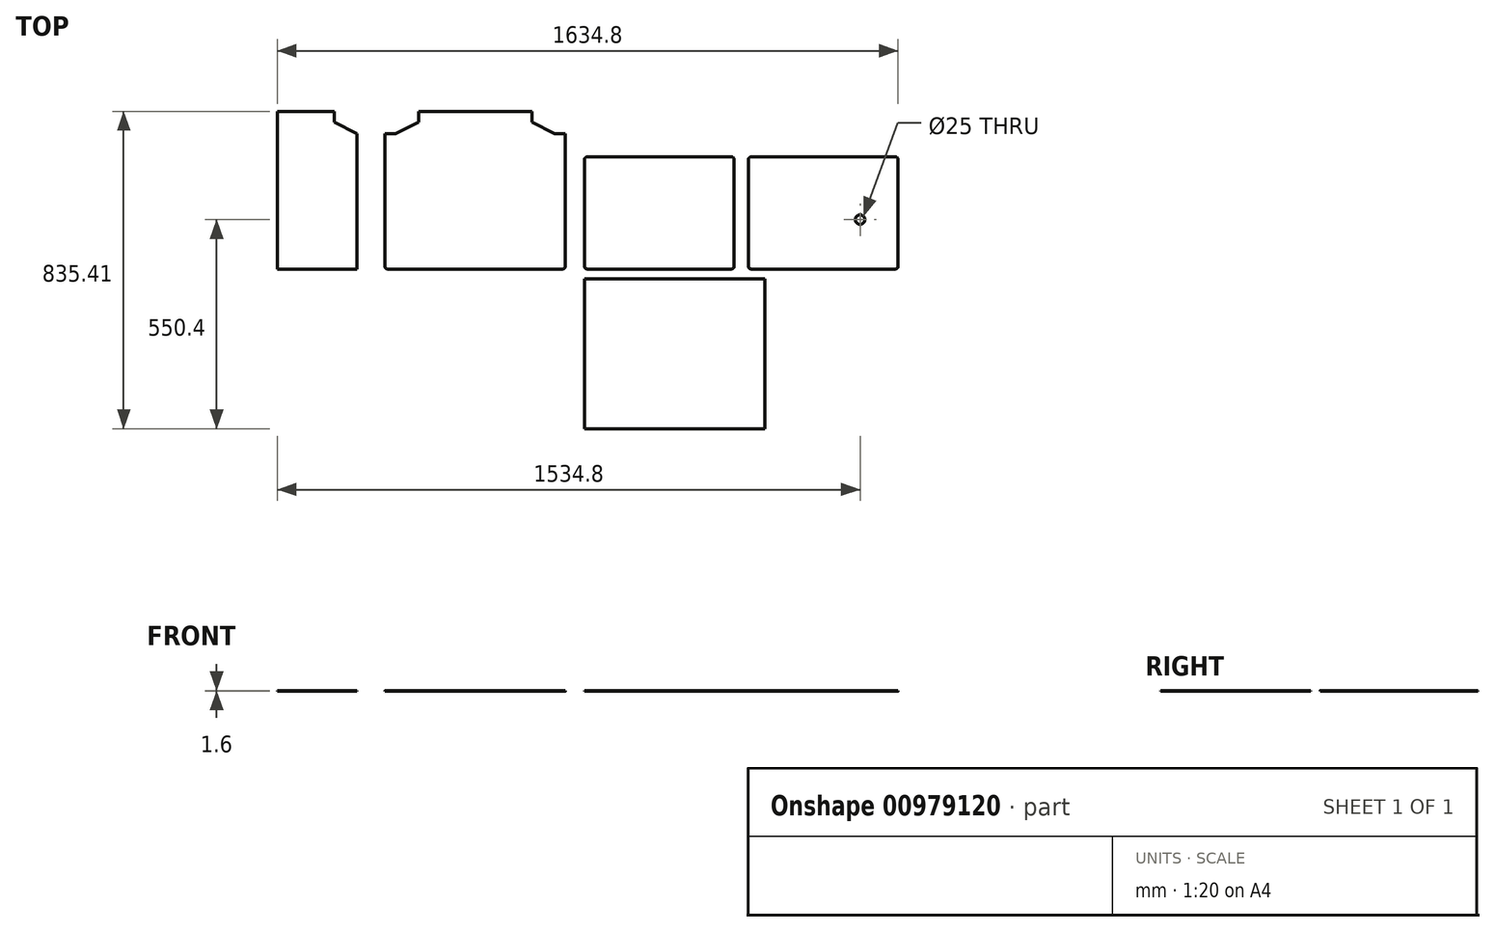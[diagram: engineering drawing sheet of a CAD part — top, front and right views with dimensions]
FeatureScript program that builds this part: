
annotation { "Feature Type Name" : "Feature", "Feature Type Description" : "" }
export const myFeature = defineFeature(function(context is Context, id is Id, definition is map)
    precondition{}
    {
        {
            var Q0;
            Q0=qCreatedBy(makeId("Top.planeOp"),FACE);
            var sketch = newSketch(context, id + "F0", { "sketchPlane" : qUnion([Q0])});
            skLineSegment(sketch, "E0.bottom", {"start": v(413.05, 295) * mm, "end": v(31.75, 295) * mm});
            skLineSegment(sketch, "E0.top", {"start": v(413.05, 0) * mm, "end": v(31.75, 0) * mm});
            skLineSegment(sketch, "E0.left", {"start": v(419.4, 288.65) * mm, "end": v(419.4, 6.35) * mm});
            skLineSegment(sketch, "E0.right", {"start": v(25.4, 288.65) * mm, "end": v(25.4, 6.35) * mm});
            skLineSegment(sketch, "E1.bottom", {"start": v(463.55, 0) * mm, "end": v(844.85, 0) * mm});
            skLineSegment(sketch, "E1.top", {"start": v(463.55, 295) * mm, "end": v(844.85, 295) * mm});
            skLineSegment(sketch, "E1.left", {"start": v(457.2, 6.35) * mm, "end": v(457.2, 288.65) * mm});
            skLineSegment(sketch, "E1.right", {"start": v(851.2, 6.35) * mm, "end": v(851.2, 288.65) * mm});
            skPoint(sketch, "E2.visualSharp", {"position": v(25.4, 295) * mm});
            skArc(sketch, "E2.filletArc", {"start": v(31.75, 295) * mm, "mid": v(27.26, 293.14) * mm, "end": v(25.4, 288.65) * mm});
            skPoint(sketch, "E3.visualSharp", {"position": v(419.4, 295) * mm});
            skArc(sketch, "E3.filletArc", {"start": v(419.4, 288.65) * mm, "mid": v(417.54, 293.14) * mm, "end": v(413.05, 295) * mm});
            skPoint(sketch, "E4.visualSharp", {"position": v(419.4, 0) * mm});
            skArc(sketch, "E4.filletArc", {"start": v(413.05, 0) * mm, "mid": v(417.54, 1.86) * mm, "end": v(419.4, 6.35) * mm});
            skPoint(sketch, "E5.visualSharp", {"position": v(25.4, 0) * mm});
            skArc(sketch, "E5.filletArc", {"start": v(25.4, 6.35) * mm, "mid": v(27.26, 1.86) * mm, "end": v(31.75, 0) * mm});
            skPoint(sketch, "E6.visualSharp", {"position": v(457.2, 0) * mm});
            skArc(sketch, "E6.filletArc", {"start": v(457.2, 6.35) * mm, "mid": v(459.06, 1.86) * mm, "end": v(463.55, 0) * mm});
            skPoint(sketch, "E7.visualSharp", {"position": v(457.2, 295) * mm});
            skArc(sketch, "E7.filletArc", {"start": v(463.55, 295) * mm, "mid": v(459.06, 293.14) * mm, "end": v(457.2, 288.65) * mm});
            skPoint(sketch, "E8.visualSharp", {"position": v(851.2, 295) * mm});
            skArc(sketch, "E8.filletArc", {"start": v(851.2, 288.65) * mm, "mid": v(849.34, 293.14) * mm, "end": v(844.85, 295) * mm});
            skPoint(sketch, "E9.visualSharp", {"position": v(851.2, 0) * mm});
            skArc(sketch, "E9.filletArc", {"start": v(844.85, 0) * mm, "mid": v(849.34, 1.86) * mm, "end": v(851.2, 6.35) * mm});
            skLineSegment(sketch, "E10", {"start": v(457.2, 0) * mm, "end": v(851.2, 0) * mm, "construction": true});
            skLineSegment(sketch, "E11", {"start": v(419.4, 0) * mm, "end": v(25.4, 0) * mm, "construction": true});
            skCircle(sketch, "E12", {"center": v(751.2, 130) * mm, "radius": 12.5 * mm});
            skLineSegment(sketch, "E13.bottom", {"start": v(-31.75, 0) * mm, "end": v(-494.05, 0) * mm});
            skLineSegment(sketch, "E13.top", {"start": v(-31.75, 415) * mm, "end": v(-494.05, 415) * mm});
            skLineSegment(sketch, "E13.left", {"start": v(-25.4, 6.35) * mm, "end": v(-25.4, 408.65) * mm});
            skLineSegment(sketch, "E13.right", {"start": v(-500.4, 6.35) * mm, "end": v(-500.4, 408.65) * mm});
            skPoint(sketch, "E14.visualSharp", {"position": v(-500.4, 415) * mm});
            skArc(sketch, "E14.filletArc", {"start": v(-494.05, 415) * mm, "mid": v(-498.54, 413.14) * mm, "end": v(-500.4, 408.65) * mm});
            skPoint(sketch, "E15.visualSharp", {"position": v(-25.4, 415) * mm});
            skArc(sketch, "E15.filletArc", {"start": v(-25.4, 408.65) * mm, "mid": v(-27.26, 413.14) * mm, "end": v(-31.75, 415) * mm});
            skPoint(sketch, "E16.visualSharp", {"position": v(-25.4, 0) * mm});
            skArc(sketch, "E16.filletArc", {"start": v(-31.75, 0) * mm, "mid": v(-27.26, 1.86) * mm, "end": v(-25.4, 6.35) * mm});
            skPoint(sketch, "E17.visualSharp", {"position": v(-500.4, 0) * mm});
            skArc(sketch, "E17.filletArc", {"start": v(-500.4, 6.35) * mm, "mid": v(-498.54, 1.86) * mm, "end": v(-494.05, 0) * mm});
            skLineSegment(sketch, "E18.bottom", {"start": v(-500.4, 415) * mm, "end": v(-412.12, 415) * mm});
            skLineSegment(sketch, "E18.top", {"start": v(-500.4, 387.06) * mm, "end": v(-412.12, 387.06) * mm});
            skLineSegment(sketch, "E18.left", {"start": v(-500.4, 415) * mm, "end": v(-500.4, 387.06) * mm});
            skLineSegment(sketch, "E18.right", {"start": v(-412.12, 415) * mm, "end": v(-412.12, 387.06) * mm});
            skLineSegment(sketch, "E19.bottom", {"start": v(-25.4, 415) * mm, "end": v(-113.67, 415) * mm});
            skLineSegment(sketch, "E19.top", {"start": v(-25.4, 387.06) * mm, "end": v(-113.67, 387.06) * mm});
            skLineSegment(sketch, "E19.left", {"start": v(-25.4, 415) * mm, "end": v(-25.4, 387.06) * mm});
            skLineSegment(sketch, "E19.right", {"start": v(-113.67, 415) * mm, "end": v(-113.67, 387.06) * mm});
            skLineSegment(sketch, "E20.bottom", {"start": v(-500.4, 387.06) * mm, "end": v(-472.46, 387.06) * mm});
            skLineSegment(sketch, "E20.top", {"start": v(-500.4, 356.58) * mm, "end": v(-472.46, 356.58) * mm});
            skLineSegment(sketch, "E20.left", {"start": v(-500.4, 387.06) * mm, "end": v(-500.4, 356.58) * mm});
            skLineSegment(sketch, "E20.right", {"start": v(-472.46, 387.06) * mm, "end": v(-472.46, 356.58) * mm});
            skLineSegment(sketch, "E21.bottom", {"start": v(-25.4, 387.06) * mm, "end": v(-53.34, 387.06) * mm});
            skLineSegment(sketch, "E21.top", {"start": v(-25.4, 356.58) * mm, "end": v(-53.34, 356.58) * mm});
            skLineSegment(sketch, "E21.left", {"start": v(-25.4, 387.06) * mm, "end": v(-25.4, 356.58) * mm});
            skLineSegment(sketch, "E21.right", {"start": v(-53.34, 387.06) * mm, "end": v(-53.34, 356.58) * mm});
            skLineSegment(sketch, "E22", {"start": v(-472.46, 356.58) * mm, "end": v(-412.12, 387.06) * mm});
            skLineSegment(sketch, "E23", {"start": v(-113.67, 387.06) * mm, "end": v(-53.34, 356.58) * mm});
            skLineSegment(sketch, "E24.bottom", {"start": v(-546.1, 0) * mm, "end": v(-1021.1, 0) * mm});
            skLineSegment(sketch, "E24.top", {"start": v(-546.1, 415.01) * mm, "end": v(-1021.1, 415.01) * mm});
            skLineSegment(sketch, "E24.left", {"start": v(-546.1, 0) * mm, "end": v(-546.1, 415.01) * mm});
            skLineSegment(sketch, "E24.right", {"start": v(-1021.1, 0) * mm, "end": v(-1021.1, 415.01) * mm});
            skLineSegment(sketch, "E25", {"start": v(-783.6, 415.01) * mm, "end": v(-783.6, 0) * mm});
            skLineSegment(sketch, "E26.bottom", {"start": v(-546.1, 415.01) * mm, "end": v(-634.38, 415.01) * mm});
            skLineSegment(sketch, "E26.top", {"start": v(-546.1, 387.07) * mm, "end": v(-634.38, 387.07) * mm});
            skLineSegment(sketch, "E26.left", {"start": v(-546.1, 415.01) * mm, "end": v(-546.1, 387.07) * mm});
            skLineSegment(sketch, "E26.right", {"start": v(-634.38, 415.01) * mm, "end": v(-634.38, 387.07) * mm});
            skLineSegment(sketch, "E27.bottom", {"start": v(-546.1, 387.07) * mm, "end": v(-574.04, 387.07) * mm});
            skLineSegment(sketch, "E27.top", {"start": v(-546.1, 356.6) * mm, "end": v(-574.04, 356.6) * mm});
            skLineSegment(sketch, "E27.left", {"start": v(-546.1, 387.07) * mm, "end": v(-546.1, 356.6) * mm});
            skLineSegment(sketch, "E27.right", {"start": v(-574.04, 387.07) * mm, "end": v(-574.04, 356.6) * mm});
            skLineSegment(sketch, "E28.bottom", {"start": v(-1021.1, 415.01) * mm, "end": v(-932.83, 415.01) * mm});
            skLineSegment(sketch, "E28.top", {"start": v(-1021.1, 387.07) * mm, "end": v(-932.83, 387.07) * mm});
            skLineSegment(sketch, "E28.left", {"start": v(-1021.1, 415.01) * mm, "end": v(-1021.1, 387.07) * mm});
            skLineSegment(sketch, "E28.right", {"start": v(-932.83, 415.01) * mm, "end": v(-932.83, 387.07) * mm});
            skLineSegment(sketch, "E29.bottom", {"start": v(-1021.1, 387.07) * mm, "end": v(-993.17, 387.07) * mm});
            skLineSegment(sketch, "E29.top", {"start": v(-1021.1, 356.6) * mm, "end": v(-993.17, 356.6) * mm});
            skLineSegment(sketch, "E29.left", {"start": v(-1021.1, 387.07) * mm, "end": v(-1021.1, 356.6) * mm});
            skLineSegment(sketch, "E29.right", {"start": v(-993.17, 387.07) * mm, "end": v(-993.17, 356.6) * mm});
            skLineSegment(sketch, "E30", {"start": v(-993.17, 356.6) * mm, "end": v(-932.83, 387.07) * mm});
            skLineSegment(sketch, "E31", {"start": v(-634.38, 387.07) * mm, "end": v(-574.04, 356.6) * mm});
            skLineSegment(sketch, "E32.bottom", {"start": v(-574.04, 356.6) * mm, "end": v(-546.1, 356.6) * mm});
            skLineSegment(sketch, "E32.top", {"start": v(-574.04, 0) * mm, "end": v(-546.1, 0) * mm});
            skLineSegment(sketch, "E32.left", {"start": v(-574.04, 356.6) * mm, "end": v(-574.04, 0) * mm});
            skLineSegment(sketch, "E32.right", {"start": v(-546.1, 356.6) * mm, "end": v(-546.1, 0) * mm});
            skLineSegment(sketch, "E33.bottom", {"start": v(25.4, -25.4) * mm, "end": v(500.4, -25.4) * mm});
            skLineSegment(sketch, "E33.top", {"start": v(25.4, -420.4) * mm, "end": v(500.4, -420.4) * mm});
            skLineSegment(sketch, "E33.left", {"start": v(25.4, -25.4) * mm, "end": v(25.4, -420.4) * mm});
            skLineSegment(sketch, "E33.right", {"start": v(500.4, -25.4) * mm, "end": v(500.4, -420.4) * mm});
            skSolve(sketch);
        }
        {
            var Q0;
            Q0=makeQuery(id+"F0.imprint","IMPRINT",FACE,{"disambiguationData":[TD([[makeQuery(id+"F0.imprint","IMPRINT",EDGE,{"derivedFrom":sQuery(id+"F0.wireOp",EDGE,"E0.bottom")}),1.0]])]});
            var Q1;
            Q1=makeQuery(id+"F0.imprint","IMPRINT",FACE,{"disambiguationData":[TD([[makeQuery(id+"F0.imprint","IMPRINT",EDGE,{"derivedFrom":sQuery(id+"F0.wireOp",EDGE,"E1.bottom")}),1.0]])]});
            var Q2;
            Q2=makeQuery(id+"F0.imprint","IMPRINT",FACE,{"disambiguationData":[TD([[makeQuery(id+"F0.imprint","IMPRINT",EDGE,{"derivedFrom":sQuery(id+"F0.wireOp",EDGE,"E13.bottom")}),-1.0]])]});
            var Q3;
            {var subQ2=sQuery(id+"F0.wireOp",EDGE,"E25");Q3=makeQuery(id+"F0.imprint","IMPRINT",FACE,{"disambiguationData":[TD([[makeQuery(id+"F0.imprint","IMPRINT",EDGE,{"derivedFrom":subQ2}),1.0]])]});}
            var Q4;
            Q4=makeQuery(id+"F0.imprint","IMPRINT",FACE,{"disambiguationData":[TD([[makeQuery(id+"F0.imprint","IMPRINT",EDGE,{"derivedFrom":sQuery(id+"F0.wireOp",EDGE,"E33.bottom")}),-1.0]])]});
            extrude(context, id + "F1", {"entities" : qUnion([Q0, Q1, Q2, Q3, Q4]), "depth" : 1.6 * mm, "offsetDistance" : 25.4 * mm});
        }
    });
